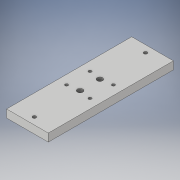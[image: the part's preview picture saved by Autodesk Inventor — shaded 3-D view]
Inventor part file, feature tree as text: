
AUTODESK INVENTOR PART (.ipt)
format: ipt  version: 2019.4 (Build 234330000, 330)  size: 137,728 bytes
history: native  units: in
note: dims shown in document units (in); Inventor stores cm internally (conversion verified against a paired STEP export)
features: sketch x4, hole x3, extrude x1, chamfer x1
ambient origin geometry x8: Origin, YZ Plane, XZ Plane, XY Plane, X Axis, Y Axis, Z Axis, Center Point
bodies: Solid1 (feature_tree)
feature tree (9):
  extrude  "Extrusion1"  Depth=1.181in
  hole  "Hole2"  [1 undecoded]
  hole  "Hole3"  [1 undecoded]
  chamfer  "Chamfer2"  Distance=0.163in
  sketch  "Sketch1"  dims[d0=3.543in d1=1.181in]
  sketch  "Sketch5"  dims[d2=0.25in d3=0.0in d33=0.118in]
  sketch  "Sketch6"  dims[d34=0.118in d35=0.197in]
  sketch  "Sketch7"  dims[d36=0.197in d37=0.097in d38=0.2in d39=0.375in d40=0.25in d41=0.5635in d42=0.22in d43=0.8108in d44=0.163in d45=0.2795in d46=0.163in d47=0.2795in d48=0.156in d49=0.38in d50=0.375in d51=0.25in d52=0.5635in d53=0.536in d54=0.8108in d55=0.18in d56=0.663in d57=0.663in d59=0.7874in d61=0.7874in d62=0.118in d63=0.3315in d64=0.3315in d65=0.8108in d66=0.5635in d67=0.25in d68=0.375in d69=0.22in d70=0.085in d71=0.028in d72=0.125in d73=45.0deg]
  hole  "Hole4"  [1 undecoded]
note: 3 required parameter values undecoded (feature->parameter linkage not recoverable at this tier; creation-order binding heuristic only, values carry confidence <= 0.55)
